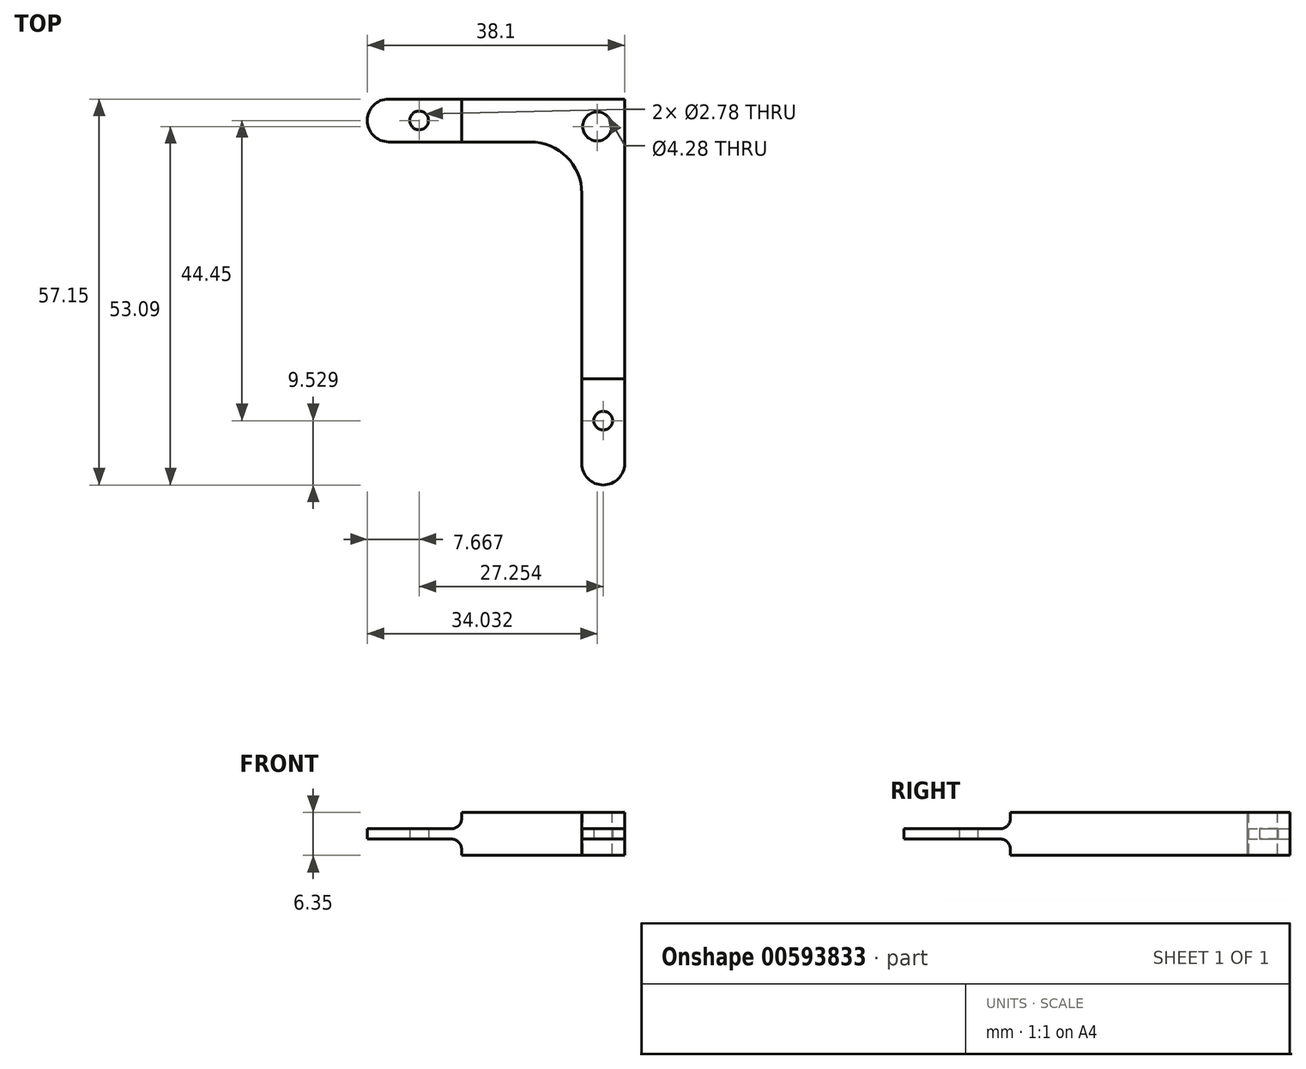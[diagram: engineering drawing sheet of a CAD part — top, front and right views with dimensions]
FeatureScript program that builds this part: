
annotation { "Feature Type Name" : "Feature", "Feature Type Description" : "" }
export const myFeature = defineFeature(function(context is Context, id is Id, definition is map)
    precondition{}
    {
        {
            var Q0;
            Q0=qCreatedBy(makeId("Top.planeOp"),FACE);
            var sketch = newSketch(context, id + "F0", { "sketchPlane" : qUnion([Q0])});
            skLineSegment(sketch, "E0", {"start": v(-29.46, 0.89) * mm, "end": v(-29.46, 0.89) * mm});
            skLineSegment(sketch, "E1", {"start": v(-26.29, -2.29) * mm, "end": v(-5.33, -2.29) * mm});
            skLineSegment(sketch, "E2", {"start": v(2.29, -9.9) * mm, "end": v(2.29, -49.91) * mm});
            skLineSegment(sketch, "E3", {"start": v(5.46, -53.09) * mm, "end": v(5.46, -53.09) * mm});
            skLineSegment(sketch, "E4", {"start": v(8.64, -49.91) * mm, "end": v(8.64, 4.06) * mm});
            skLineSegment(sketch, "E5", {"start": v(8.64, 4.06) * mm, "end": v(-26.29, 4.06) * mm});
            skPoint(sketch, "E6.visualSharp", {"position": v(2.29, -2.29) * mm});
            skArc(sketch, "E6.filletArc", {"start": v(2.29, -9.9) * mm, "mid": v(0.05, -4.52) * mm, "end": v(-5.33, -2.29) * mm});
            skPoint(sketch, "E7.visualSharp", {"position": v(-29.46, 4.06) * mm});
            skArc(sketch, "E7.filletArc", {"start": v(-26.29, 4.06) * mm, "mid": v(-28.53, 3.13) * mm, "end": v(-29.46, 0.89) * mm});
            skPoint(sketch, "E8.visualSharp", {"position": v(-29.46, -2.29) * mm});
            skArc(sketch, "E8.filletArc", {"start": v(-29.46, 0.89) * mm, "mid": v(-28.53, -1.36) * mm, "end": v(-26.29, -2.29) * mm});
            skPoint(sketch, "E9.visualSharp", {"position": v(2.29, -53.09) * mm});
            skArc(sketch, "E9.filletArc", {"start": v(2.29, -49.91) * mm, "mid": v(3.22, -52.16) * mm, "end": v(5.46, -53.09) * mm});
            skPoint(sketch, "E10.visualSharp", {"position": v(8.64, -53.09) * mm});
            skArc(sketch, "E10.filletArc", {"start": v(5.46, -53.09) * mm, "mid": v(7.7, -52.16) * mm, "end": v(8.64, -49.91) * mm});
            skCircle(sketch, "E11", {"center": v(4.57, 0) * mm, "radius": 2.14 * mm});
            skCircle(sketch, "E12", {"center": v(-21.8, 0.89) * mm, "radius": 1.39 * mm});
            skCircle(sketch, "E13", {"center": v(5.46, -43.56) * mm, "radius": 1.39 * mm});
            skSolve(sketch);
        }
        {
            var Q0;
            Q0 = qSketchRegion(id + "F0", true);
            extrude(context, id + "F1", {"entities" : qUnion([Q0]), "depth" : 6.35 * mm, "offsetDistance" : 25.4 * mm});
        }
        {
            var Q0;
            Q0=makeQuery(id+"F1.opExtrude","SWEPT_FACE",FACE,{"disambiguationData":[OSD([sQuery(id+"F0.wireOp",EDGE,"E4")])]});
            var sketch = newSketch(context, id + "F2", { "sketchPlane" : qUnion([Q0])});
            skLineSegment(sketch, "E14.0", {"start": v(-37.34, 3.94) * mm, "end": v(-55.22, 3.94) * mm});
            skLineSegment(sketch, "E15.0", {"start": v(-37.34, 2.41) * mm, "end": v(-55.22, 2.41) * mm});
            skLineSegment(sketch, "E16", {"start": v(-55.22, 7.1) * mm, "end": v(-55.22, 3.94) * mm});
            skLineSegment(sketch, "E17.trimOffspring", {"start": v(-55.22, 2.41) * mm, "end": v(-55.22, -1.23) * mm});
            skLineSegment(sketch, "E18", {"start": v(-55.22, 7.1) * mm, "end": v(-37.34, 7.1) * mm});
            skLineSegment(sketch, "E19", {"start": v(-55.22, -1.23) * mm, "end": v(-37.34, -1.23) * mm});
            skLineSegment(sketch, "E20.0", {"start": v(-37.34, 7.1) * mm, "end": v(-37.34, 3.94) * mm});
            skLineSegment(sketch, "E21.trimOffspring", {"start": v(-37.34, 2.41) * mm, "end": v(-37.34, -1.23) * mm});
            skSolve(sketch);
        }
        {
            var Q0;
            Q0 = qSketchRegion(id + "F2", true);
            extrude(context, id + "F3", {"entities" : qUnion([Q0]), "operationType" : NewBodyOperationType.REMOVE, "endBound" : BoundingType.THROUGH_ALL, "oppositeDirection" : true, "depth" : 25.4 * mm, "offsetDistance" : 25.4 * mm});
        }
        {
            var Q0;
            Q0=makeQuery(id+"F1.opExtrude","SWEPT_FACE",FACE,{"disambiguationData":[OSD([sQuery(id+"F0.wireOp",EDGE,"E5")])]});
            var sketch = newSketch(context, id + "F4", { "sketchPlane" : qUnion([Q0])});
            skLineSegment(sketch, "E22.0", {"start": v(15.5, 6.35) * mm, "end": v(15.5, 3.94) * mm});
            skLineSegment(sketch, "E23", {"start": v(15.5, 6.35) * mm, "end": v(33.46, 6.35) * mm});
            skLineSegment(sketch, "E24", {"start": v(15.5, 0) * mm, "end": v(33.46, 0) * mm});
            skLineSegment(sketch, "E25.0", {"start": v(15.5, 3.94) * mm, "end": v(33.46, 3.94) * mm});
            skLineSegment(sketch, "E26.0", {"start": v(15.5, 2.41) * mm, "end": v(33.46, 2.41) * mm});
            skLineSegment(sketch, "E27", {"start": v(33.46, 6.35) * mm, "end": v(33.46, 3.94) * mm});
            skLineSegment(sketch, "E28.trimOffspring", {"start": v(15.5, 2.41) * mm, "end": v(15.5, 0) * mm});
            skLineSegment(sketch, "E29.trimOffspring", {"start": v(33.46, 2.41) * mm, "end": v(33.46, 0) * mm});
            skSolve(sketch);
        }
        {
            var Q0;
            Q0 = qSketchRegion(id + "F4", true);
            extrude(context, id + "F5", {"entities" : qUnion([Q0]), "operationType" : NewBodyOperationType.REMOVE, "endBound" : BoundingType.THROUGH_ALL, "oppositeDirection" : true, "depth" : 25.4 * mm, "offsetDistance" : 25.4 * mm});
        }
        {
            var Q0;
            Q0=makeQuery(id+"F5.boolean.opBoolean","COPY",EDGE,{"derivedFrom":makeQuery(id+"F5.opExtrude","SWEPT_EDGE",EDGE,{"disambiguationData":[OSD([sQuery(id+"F4.wireOp",EDGE,"E22.0"),sQuery(id+"F4.wireOp",EDGE,"E25.0")])]})});
            var Q1;
            Q1=makeQuery(id+"F5.boolean.opBoolean","COPY",EDGE,{"derivedFrom":makeQuery(id+"F5.opExtrude","SWEPT_EDGE",EDGE,{"disambiguationData":[OSD([sQuery(id+"F4.wireOp",EDGE,"E26.0"),sQuery(id+"F4.wireOp",EDGE,"E28.trimOffspring")])]})});
            var Q2;
            Q2=makeQuery(id+"F3.boolean.opBoolean","COPY",EDGE,{"derivedFrom":makeQuery(id+"F3.opExtrude","SWEPT_EDGE",EDGE,{"disambiguationData":[OSD([sQuery(id+"F2.wireOp",EDGE,"E14.0"),sQuery(id+"F2.wireOp",EDGE,"E20.0")])]})});
            var Q3;
            Q3=makeQuery(id+"F3.boolean.opBoolean","COPY",EDGE,{"derivedFrom":makeQuery(id+"F3.opExtrude","SWEPT_EDGE",EDGE,{"disambiguationData":[OSD([sQuery(id+"F2.wireOp",EDGE,"E15.0"),sQuery(id+"F2.wireOp",EDGE,"E21.trimOffspring")])]})});
            fillet(context, id + "F6", {"entities" : qUnion([Q0, Q1, Q2, Q3]), "radius" : 1.52 * mm, "tangentPropagation" : true, "allowEdgeOverflow" : false});
        }
    });
